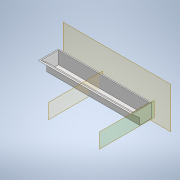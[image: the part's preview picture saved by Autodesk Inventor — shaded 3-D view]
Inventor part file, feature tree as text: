
AUTODESK INVENTOR PART (.ipt)
format: ipt  version: 2022 (Build 260153000, 153)  size: 134,656 bytes
history: native  units: in
note: dims shown in document units (in); Inventor stores cm internally (conversion verified against a paired STEP export)
features: reference x7, other x6, plane x3, extrude x3, sketch x3, shell x1
ambient origin geometry x8: Origin, YZ Plane, XZ Plane, XY Plane, X Axis, Y Axis, Z Axis, Center Point
bodies: Solid1 (feature_tree)
feature tree (23):
  plane  "Work Plane1"
  plane  "Work Plane2"
  plane  "Work Plane3"
  extrude  "Extrusion1"  Depth=0.3937in
  shell  "Shell1"  Thickness=0.3937in
  extrude  "Extrusion2"  Depth=0.1969in
  extrude  "Extrusion3"  Depth=0.1969in
  sketch  "Sketch2"  dims[d2=0.0039in d3=0.0079in d5=0.3937in d6=0.0in]
  reference  "Reference5"
  reference  "Reference6"
  reference  "Reference7"
  reference  "Reference8"
  reference  "Reference9"
  sketch  "Sketch3"  dims[d7=0.1969in d8=0.1969in]
  reference  "Reference10"
  sketch  "Sketch4"  dims[d9=0.3937in d10=0.0in d12=0.1969in d13=0.1969in d14=0.0in d15=0.0in d16=0.0197in]
  reference  "Reference11"
  other  "Linear Rail Assembly.iam"
  other  "dilution system bracket:1"
  other  "Printer Assembly:1"
  other  "Base_v7:1"
  other  "Control_Panel_v4:1"
  other  "dilution system bracket_MIR:1"
